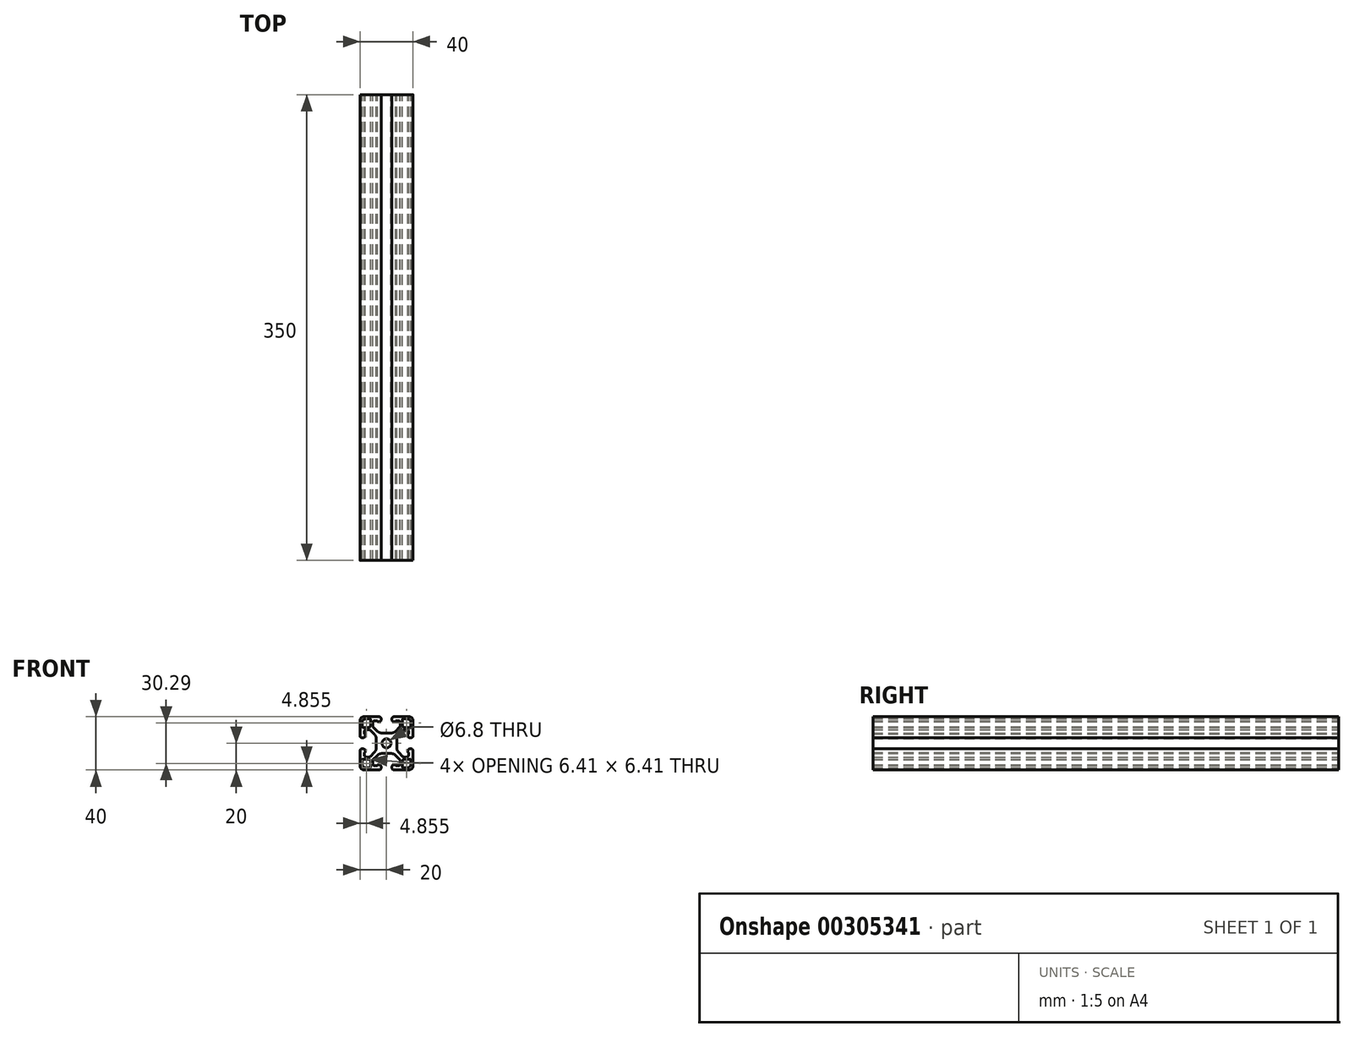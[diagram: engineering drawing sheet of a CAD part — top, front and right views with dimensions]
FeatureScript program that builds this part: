
annotation { "Feature Type Name" : "Feature", "Feature Type Description" : "" }
export const myFeature = defineFeature(function(context is Context, id is Id, definition is map)
    precondition{}
    {
        {
            var Q0;
            Q0=qCreatedBy(makeId("Front.planeOp"),FACE);
            var sketch = newSketch(context, id + "F0", { "sketchPlane" : qUnion([Q0])});
            skLineSegment(sketch, "E0", {"start": v(15.55, 18.35) * mm, "end": v(12.57, 18.35) * mm});
            skArc(sketch, "E1", {"start": v(12.57, 18.35) * mm, "mid": v(12.12, 18.17) * mm, "end": v(11.94, 17.72) * mm});
            skLineSegment(sketch, "E2", {"start": v(11.94, 17.72) * mm, "end": v(11.94, 13.2) * mm});
            skArc(sketch, "E3", {"start": v(11.94, 13.2) * mm, "mid": v(12.31, 12.31) * mm, "end": v(13.21, 11.94) * mm});
            skLineSegment(sketch, "E4", {"start": v(13.21, 11.94) * mm, "end": v(17.72, 11.94) * mm});
            skArc(sketch, "E5", {"start": v(17.72, 11.94) * mm, "mid": v(18.17, 12.12) * mm, "end": v(18.35, 12.57) * mm});
            skLineSegment(sketch, "E6", {"start": v(18.35, 12.57) * mm, "end": v(18.35, 15.55) * mm});
            skArc(sketch, "E7", {"start": v(18.35, 15.55) * mm, "mid": v(17.53, 17.53) * mm, "end": v(15.55, 18.35) * mm});
            skCircle(sketch, "E8", {"center": v(0, 0) * mm, "radius": 3.4 * mm});
            skLineSegment(sketch, "E9", {"start": v(-15.55, -18.35) * mm, "end": v(-12.57, -18.35) * mm});
            skArc(sketch, "E10", {"start": v(-12.57, -18.35) * mm, "mid": v(-12.12, -18.17) * mm, "end": v(-11.94, -17.72) * mm});
            skLineSegment(sketch, "E11", {"start": v(-11.94, -17.72) * mm, "end": v(-11.94, -13.2) * mm});
            skArc(sketch, "E12", {"start": v(-11.94, -13.2) * mm, "mid": v(-12.31, -12.31) * mm, "end": v(-13.21, -11.94) * mm});
            skLineSegment(sketch, "E13", {"start": v(-13.21, -11.94) * mm, "end": v(-17.72, -11.94) * mm});
            skArc(sketch, "E14", {"start": v(-17.72, -11.94) * mm, "mid": v(-18.17, -12.12) * mm, "end": v(-18.35, -12.57) * mm});
            skLineSegment(sketch, "E15", {"start": v(-18.35, -12.57) * mm, "end": v(-18.35, -15.55) * mm});
            skArc(sketch, "E16", {"start": v(-18.35, -15.55) * mm, "mid": v(-17.53, -17.53) * mm, "end": v(-15.55, -18.35) * mm});
            skLineSegment(sketch, "E17", {"start": v(17.72, -11.94) * mm, "end": v(13.21, -11.94) * mm});
            skArc(sketch, "E18", {"start": v(13.21, -11.94) * mm, "mid": v(12.31, -12.31) * mm, "end": v(11.94, -13.2) * mm});
            skLineSegment(sketch, "E19", {"start": v(11.94, -13.2) * mm, "end": v(11.94, -17.72) * mm});
            skArc(sketch, "E20", {"start": v(11.94, -17.72) * mm, "mid": v(12.12, -18.17) * mm, "end": v(12.57, -18.35) * mm});
            skLineSegment(sketch, "E21", {"start": v(12.57, -18.35) * mm, "end": v(15.55, -18.35) * mm});
            skArc(sketch, "E22", {"start": v(15.55, -18.35) * mm, "mid": v(17.53, -17.53) * mm, "end": v(18.35, -15.55) * mm});
            skLineSegment(sketch, "E23", {"start": v(18.35, -15.55) * mm, "end": v(18.35, -12.57) * mm});
            skArc(sketch, "E24", {"start": v(18.35, -12.57) * mm, "mid": v(18.17, -12.12) * mm, "end": v(17.72, -11.94) * mm});
            skArc(sketch, "E25", {"start": v(-18.35, 12.57) * mm, "mid": v(-18.17, 12.12) * mm, "end": v(-17.72, 11.94) * mm});
            skLineSegment(sketch, "E26", {"start": v(-17.72, 11.94) * mm, "end": v(-13.21, 11.94) * mm});
            skArc(sketch, "E27", {"start": v(-13.21, 11.94) * mm, "mid": v(-12.31, 12.31) * mm, "end": v(-11.94, 13.2) * mm});
            skLineSegment(sketch, "E28", {"start": v(-11.94, 13.2) * mm, "end": v(-11.94, 17.72) * mm});
            skArc(sketch, "E29", {"start": v(-11.94, 17.72) * mm, "mid": v(-12.12, 18.17) * mm, "end": v(-12.57, 18.35) * mm});
            skLineSegment(sketch, "E30", {"start": v(-12.57, 18.35) * mm, "end": v(-15.55, 18.35) * mm});
            skArc(sketch, "E31", {"start": v(-15.55, 18.35) * mm, "mid": v(-17.53, 17.53) * mm, "end": v(-18.35, 15.55) * mm});
            skLineSegment(sketch, "E32", {"start": v(-18.35, 15.55) * mm, "end": v(-18.35, 12.57) * mm});
            skLineSegment(sketch, "E33", {"start": v(7.69, -3.36) * mm, "end": v(7.69, 3.36) * mm});
            skArc(sketch, "E34", {"start": v(9.07, 6.71) * mm, "mid": v(8.05, 5.17) * mm, "end": v(7.69, 3.36) * mm});
            skLineSegment(sketch, "E35", {"start": v(9.07, 6.71) * mm, "end": v(12.37, 10.02) * mm});
            skArc(sketch, "E36", {"start": v(13, 10.28) * mm, "mid": v(12.66, 10.21) * mm, "end": v(12.37, 10.02) * mm});
            skLineSegment(sketch, "E37", {"start": v(13, 10.28) * mm, "end": v(15.3, 10.28) * mm});
            skArc(sketch, "E38", {"start": v(16.57, 9) * mm, "mid": v(16.2, 9.9) * mm, "end": v(15.3, 10.28) * mm});
            skLineSegment(sketch, "E39", {"start": v(16.57, 9) * mm, "end": v(16.57, 6.9) * mm});
            skLineSegment(sketch, "E40", {"start": v(16.57, 6.9) * mm, "end": v(15.94, 6.9) * mm});
            skLineSegment(sketch, "E41", {"start": v(15.94, 6.9) * mm, "end": v(15.94, 5.76) * mm});
            skArc(sketch, "E42", {"start": v(15.94, 5.76) * mm, "mid": v(16.4, 4.65) * mm, "end": v(17.5, 4.19) * mm});
            skLineSegment(sketch, "E43", {"start": v(17.5, 4.19) * mm, "end": v(18.43, 4.19) * mm});
            skArc(sketch, "E44", {"start": v(18.43, 4.19) * mm, "mid": v(19.54, 4.65) * mm, "end": v(20, 5.76) * mm});
            skLineSegment(sketch, "E45", {"start": v(20, 5.76) * mm, "end": v(20, 16.83) * mm});
            skArc(sketch, "E46", {"start": v(20, 16.83) * mm, "mid": v(19.07, 19.07) * mm, "end": v(16.83, 20) * mm});
            skLineSegment(sketch, "E47", {"start": v(16.83, 20) * mm, "end": v(5.63, 20) * mm});
            skArc(sketch, "E48", {"start": v(5.63, 20) * mm, "mid": v(4.52, 19.54) * mm, "end": v(4.06, 18.43) * mm});
            skLineSegment(sketch, "E49", {"start": v(4.06, 18.43) * mm, "end": v(4.06, 17.7) * mm});
            skArc(sketch, "E50", {"start": v(4.06, 17.7) * mm, "mid": v(4.52, 16.59) * mm, "end": v(5.63, 16.13) * mm});
            skLineSegment(sketch, "E51", {"start": v(5.63, 16.13) * mm, "end": v(6.78, 16.13) * mm});
            skLineSegment(sketch, "E52", {"start": v(6.78, 16.13) * mm, "end": v(6.78, 16.89) * mm});
            skLineSegment(sketch, "E53", {"start": v(6.78, 16.89) * mm, "end": v(9.01, 16.89) * mm});
            skArc(sketch, "E54", {"start": v(10.28, 15.62) * mm, "mid": v(9.91, 16.51) * mm, "end": v(9.01, 16.89) * mm});
            skLineSegment(sketch, "E55", {"start": v(10.28, 15.62) * mm, "end": v(10.28, 12.92) * mm});
            skArc(sketch, "E56", {"start": v(10.17, 12.48) * mm, "mid": v(10.25, 12.7) * mm, "end": v(10.29, 12.92) * mm});
            skLineSegment(sketch, "E57", {"start": v(10.17, 12.48) * mm, "end": v(6.77, 9.08) * mm});
            skArc(sketch, "E58", {"start": v(3.4, 7.69) * mm, "mid": v(5.23, 8.05) * mm, "end": v(6.77, 9.08) * mm});
            skLineSegment(sketch, "E59", {"start": v(3.4, 7.69) * mm, "end": v(-3.4, 7.69) * mm});
            skArc(sketch, "E60", {"start": v(-6.77, 9.08) * mm, "mid": v(-5.23, 8.05) * mm, "end": v(-3.4, 7.69) * mm});
            skLineSegment(sketch, "E61", {"start": v(-6.77, 9.08) * mm, "end": v(-10.17, 12.48) * mm});
            skArc(sketch, "E62", {"start": v(-10.29, 12.92) * mm, "mid": v(-10.25, 12.7) * mm, "end": v(-10.17, 12.48) * mm});
            skLineSegment(sketch, "E63", {"start": v(-10.28, 12.92) * mm, "end": v(-10.28, 15.62) * mm});
            skArc(sketch, "E64", {"start": v(-9.01, 16.89) * mm, "mid": v(-9.91, 16.51) * mm, "end": v(-10.28, 15.62) * mm});
            skLineSegment(sketch, "E65", {"start": v(-9.01, 16.89) * mm, "end": v(-6.78, 16.89) * mm});
            skLineSegment(sketch, "E66", {"start": v(-6.78, 16.89) * mm, "end": v(-6.78, 16.13) * mm});
            skLineSegment(sketch, "E67", {"start": v(-6.78, 16.13) * mm, "end": v(-5.63, 16.13) * mm});
            skArc(sketch, "E68", {"start": v(-5.63, 16.13) * mm, "mid": v(-4.52, 16.59) * mm, "end": v(-4.06, 17.7) * mm});
            skLineSegment(sketch, "E69", {"start": v(-4.06, 17.7) * mm, "end": v(-4.06, 18.43) * mm});
            skArc(sketch, "E70", {"start": v(-4.06, 18.43) * mm, "mid": v(-4.52, 19.54) * mm, "end": v(-5.63, 20) * mm});
            skLineSegment(sketch, "E71", {"start": v(-5.63, 20) * mm, "end": v(-16.83, 20) * mm});
            skArc(sketch, "E72", {"start": v(-16.83, 20) * mm, "mid": v(-19.07, 19.07) * mm, "end": v(-20, 16.83) * mm});
            skLineSegment(sketch, "E73", {"start": v(-20, 16.83) * mm, "end": v(-20, 5.76) * mm});
            skArc(sketch, "E74", {"start": v(-20, 5.76) * mm, "mid": v(-19.54, 4.65) * mm, "end": v(-18.43, 4.19) * mm});
            skLineSegment(sketch, "E75", {"start": v(-18.43, 4.19) * mm, "end": v(-17.5, 4.19) * mm});
            skArc(sketch, "E76", {"start": v(-17.5, 4.19) * mm, "mid": v(-16.4, 4.65) * mm, "end": v(-15.94, 5.76) * mm});
            skLineSegment(sketch, "E77", {"start": v(-15.94, 5.76) * mm, "end": v(-15.94, 6.9) * mm});
            skLineSegment(sketch, "E78", {"start": v(-15.94, 6.9) * mm, "end": v(-16.57, 6.9) * mm});
            skLineSegment(sketch, "E79", {"start": v(-16.57, 6.9) * mm, "end": v(-16.57, 9) * mm});
            skArc(sketch, "E80", {"start": v(-15.3, 10.28) * mm, "mid": v(-16.2, 9.9) * mm, "end": v(-16.57, 9) * mm});
            skLineSegment(sketch, "E81", {"start": v(-15.3, 10.28) * mm, "end": v(-13, 10.28) * mm});
            skArc(sketch, "E82", {"start": v(-12.37, 10.02) * mm, "mid": v(-12.66, 10.21) * mm, "end": v(-13, 10.28) * mm});
            skLineSegment(sketch, "E83", {"start": v(-12.37, 10.02) * mm, "end": v(-9.07, 6.71) * mm});
            skArc(sketch, "E84", {"start": v(-7.69, 3.36) * mm, "mid": v(-8.05, 5.17) * mm, "end": v(-9.07, 6.71) * mm});
            skLineSegment(sketch, "E85", {"start": v(-7.69, 3.36) * mm, "end": v(-7.69, -3.36) * mm});
            skArc(sketch, "E86", {"start": v(-9.07, -6.71) * mm, "mid": v(-8.05, -5.17) * mm, "end": v(-7.69, -3.36) * mm});
            skLineSegment(sketch, "E87", {"start": v(-9.07, -6.71) * mm, "end": v(-12.37, -10.02) * mm});
            skArc(sketch, "E88", {"start": v(-13, -10.28) * mm, "mid": v(-12.66, -10.21) * mm, "end": v(-12.37, -10.02) * mm});
            skLineSegment(sketch, "E89", {"start": v(-13, -10.28) * mm, "end": v(-15.3, -10.28) * mm});
            skArc(sketch, "E90", {"start": v(-16.57, -9) * mm, "mid": v(-16.2, -9.9) * mm, "end": v(-15.3, -10.28) * mm});
            skLineSegment(sketch, "E91", {"start": v(-16.57, -9) * mm, "end": v(-16.57, -6.9) * mm});
            skLineSegment(sketch, "E92", {"start": v(-16.57, -6.9) * mm, "end": v(-15.94, -6.9) * mm});
            skLineSegment(sketch, "E93", {"start": v(-15.94, -6.9) * mm, "end": v(-15.94, -5.76) * mm});
            skArc(sketch, "E94", {"start": v(-15.94, -5.76) * mm, "mid": v(-16.4, -4.65) * mm, "end": v(-17.5, -4.19) * mm});
            skLineSegment(sketch, "E95", {"start": v(-17.5, -4.19) * mm, "end": v(-18.43, -4.19) * mm});
            skArc(sketch, "E96", {"start": v(-18.43, -4.19) * mm, "mid": v(-19.54, -4.65) * mm, "end": v(-20, -5.76) * mm});
            skLineSegment(sketch, "E97", {"start": v(-20, -5.76) * mm, "end": v(-20, -16.83) * mm});
            skArc(sketch, "E98", {"start": v(-20, -16.83) * mm, "mid": v(-19.07, -19.07) * mm, "end": v(-16.83, -20) * mm});
            skLineSegment(sketch, "E99", {"start": v(-16.83, -20) * mm, "end": v(-5.63, -20) * mm});
            skArc(sketch, "E100", {"start": v(-5.63, -20) * mm, "mid": v(-4.52, -19.54) * mm, "end": v(-4.06, -18.43) * mm});
            skLineSegment(sketch, "E101", {"start": v(-4.06, -18.43) * mm, "end": v(-4.06, -17.7) * mm});
            skArc(sketch, "E102", {"start": v(-4.06, -17.7) * mm, "mid": v(-4.52, -16.59) * mm, "end": v(-5.63, -16.13) * mm});
            skLineSegment(sketch, "E103", {"start": v(-5.63, -16.13) * mm, "end": v(-6.78, -16.13) * mm});
            skLineSegment(sketch, "E104", {"start": v(-6.78, -16.13) * mm, "end": v(-6.78, -16.89) * mm});
            skLineSegment(sketch, "E105", {"start": v(-6.78, -16.89) * mm, "end": v(-9.01, -16.89) * mm});
            skArc(sketch, "E106", {"start": v(-10.28, -15.62) * mm, "mid": v(-9.91, -16.51) * mm, "end": v(-9.01, -16.89) * mm});
            skLineSegment(sketch, "E107", {"start": v(-10.28, -15.62) * mm, "end": v(-10.28, -12.92) * mm});
            skArc(sketch, "E108", {"start": v(-10.17, -12.48) * mm, "mid": v(-10.25, -12.7) * mm, "end": v(-10.29, -12.92) * mm});
            skLineSegment(sketch, "E109", {"start": v(-10.17, -12.48) * mm, "end": v(-6.77, -9.08) * mm});
            skArc(sketch, "E110", {"start": v(-3.4, -7.69) * mm, "mid": v(-5.23, -8.05) * mm, "end": v(-6.77, -9.08) * mm});
            skLineSegment(sketch, "E111", {"start": v(-3.4, -7.69) * mm, "end": v(3.4, -7.69) * mm});
            skArc(sketch, "E112", {"start": v(6.77, -9.08) * mm, "mid": v(5.23, -8.05) * mm, "end": v(3.4, -7.69) * mm});
            skLineSegment(sketch, "E113", {"start": v(6.77, -9.08) * mm, "end": v(10.17, -12.48) * mm});
            skArc(sketch, "E114", {"start": v(10.29, -12.92) * mm, "mid": v(10.25, -12.7) * mm, "end": v(10.17, -12.48) * mm});
            skLineSegment(sketch, "E115", {"start": v(10.28, -12.92) * mm, "end": v(10.28, -15.62) * mm});
            skArc(sketch, "E116", {"start": v(9.01, -16.89) * mm, "mid": v(9.91, -16.51) * mm, "end": v(10.28, -15.62) * mm});
            skLineSegment(sketch, "E117", {"start": v(9.01, -16.89) * mm, "end": v(6.78, -16.89) * mm});
            skLineSegment(sketch, "E118", {"start": v(6.78, -16.89) * mm, "end": v(6.78, -16.13) * mm});
            skLineSegment(sketch, "E119", {"start": v(6.78, -16.13) * mm, "end": v(5.63, -16.13) * mm});
            skArc(sketch, "E120", {"start": v(5.63, -16.13) * mm, "mid": v(4.52, -16.59) * mm, "end": v(4.06, -17.7) * mm});
            skLineSegment(sketch, "E121", {"start": v(4.06, -17.7) * mm, "end": v(4.06, -18.43) * mm});
            skArc(sketch, "E122", {"start": v(4.06, -18.43) * mm, "mid": v(4.52, -19.54) * mm, "end": v(5.63, -20) * mm});
            skLineSegment(sketch, "E123", {"start": v(5.63, -20) * mm, "end": v(16.83, -20) * mm});
            skArc(sketch, "E124", {"start": v(16.83, -20) * mm, "mid": v(19.07, -19.07) * mm, "end": v(20, -16.83) * mm});
            skLineSegment(sketch, "E125", {"start": v(20, -16.83) * mm, "end": v(20, -5.76) * mm});
            skArc(sketch, "E126", {"start": v(20, -5.76) * mm, "mid": v(19.54, -4.65) * mm, "end": v(18.43, -4.19) * mm});
            skLineSegment(sketch, "E127", {"start": v(18.43, -4.19) * mm, "end": v(17.5, -4.19) * mm});
            skArc(sketch, "E128", {"start": v(17.5, -4.19) * mm, "mid": v(16.4, -4.65) * mm, "end": v(15.94, -5.76) * mm});
            skLineSegment(sketch, "E129", {"start": v(15.94, -5.76) * mm, "end": v(15.94, -6.9) * mm});
            skLineSegment(sketch, "E130", {"start": v(15.94, -6.9) * mm, "end": v(16.57, -6.9) * mm});
            skLineSegment(sketch, "E131", {"start": v(16.57, -6.9) * mm, "end": v(16.57, -9) * mm});
            skArc(sketch, "E132", {"start": v(15.3, -10.28) * mm, "mid": v(16.2, -9.9) * mm, "end": v(16.57, -9) * mm});
            skLineSegment(sketch, "E133", {"start": v(15.3, -10.28) * mm, "end": v(13, -10.28) * mm});
            skArc(sketch, "E134", {"start": v(12.37, -10.02) * mm, "mid": v(12.66, -10.21) * mm, "end": v(13, -10.28) * mm});
            skLineSegment(sketch, "E135", {"start": v(12.37, -10.02) * mm, "end": v(9.07, -6.71) * mm});
            skArc(sketch, "E136", {"start": v(7.69, -3.36) * mm, "mid": v(8.05, -5.17) * mm, "end": v(9.07, -6.71) * mm});
            skLineSegment(sketch, "E137", {"start": v(0, 0) * mm, "end": v(0, 2.54) * mm});
            skLineSegment(sketch, "E138", {"start": v(0, 0) * mm, "end": v(-2.54, 0) * mm});
            skLineSegment(sketch, "E139", {"start": v(0, 0) * mm, "end": v(0, -2.54) * mm});
            skLineSegment(sketch, "E140", {"start": v(0, 0) * mm, "end": v(2.54, 0) * mm});
            skLineSegment(sketch, "E141", {"start": v(0, 5.08) * mm, "end": v(0, 5.94) * mm});
            skLineSegment(sketch, "E142", {"start": v(-5.08, 0) * mm, "end": v(-5.94, 0) * mm});
            skLineSegment(sketch, "E143", {"start": v(0, -5.08) * mm, "end": v(0, -5.94) * mm});
            skLineSegment(sketch, "E144", {"start": v(5.08, 0) * mm, "end": v(5.94, 0) * mm});
            skSolve(sketch);
        }
        {
            var Q0;
            Q0 = qSketchRegion(id + "F0", true);
            extrude(context, id + "F1", {"entities" : qUnion([Q0]), "depth" : 350 * mm});
        }
    });
